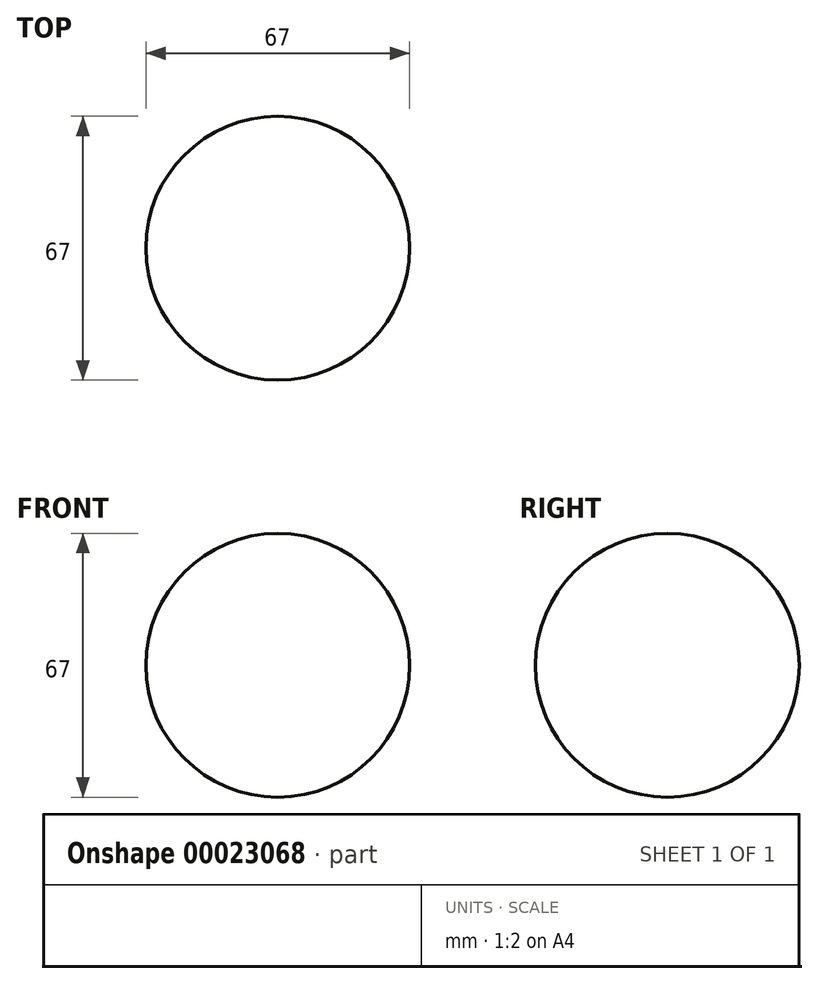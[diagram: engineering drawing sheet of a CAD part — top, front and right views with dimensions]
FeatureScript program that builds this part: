
annotation { "Feature Type Name" : "Feature", "Feature Type Description" : "" }
export const myFeature = defineFeature(function(context is Context, id is Id, definition is map)
    precondition{}
    {
        {
            var Q0;
            Q0=qCreatedBy(makeId("Front.planeOp"),FACE);
            var sketch = newSketch(context, id + "F0", { "sketchPlane" : qUnion([Q0])});
            skLineSegment(sketch, "E0.bottom", {"start": v(-22.5, 13) * mm, "end": v(22.5, 13) * mm});
            skLineSegment(sketch, "E0.top", {"start": v(-22.5, -13) * mm, "end": v(22.5, -13) * mm});
            skLineSegment(sketch, "E0.left", {"start": v(-22.5, 13) * mm, "end": v(-22.5, -13) * mm});
            skLineSegment(sketch, "E0.right", {"start": v(22.5, 13) * mm, "end": v(22.5, -13) * mm});
            skPoint(sketch, "E1", {"position": v(0, 13) * mm});
            skPoint(sketch, "E2", {"position": v(22.5, 0) * mm});
            skArc(sketch, "E3", {"start": v(0, 33.5) * mm, "mid": v(-33.5, 0) * mm, "end": v(0, -33.5) * mm});
            skLineSegment(sketch, "E4", {"start": v(0, 33.5) * mm, "end": v(0, -33.5) * mm});
            skSolve(sketch);
        }
        {
            var Q0;
            {var subQ1=sQuery(id+"F0.wireOp",EDGE,"E0.left");Q0=makeQuery(id+"F0.imprint","IMPRINT",FACE,{"disambiguationData":[TD([[makeQuery(id+"F0.imprint","IMPRINT",EDGE,{"derivedFrom":subQ1}),-1.0]])]});}
            var Q1;
            {var subQ0=sQuery(id+"F0.wireOp",EDGE,"E0.left");Q1=makeQuery(id+"F0.imprint","IMPRINT",FACE,{"disambiguationData":[TD([[makeQuery(id+"F0.imprint","IMPRINT",EDGE,{"derivedFrom":subQ0}),1.0]])]});}
            var Q2;
            Q2=sQuery(id+"F0.wireOp",EDGE,"E4");
            revolve(context, id + "F1", {"entities" : qUnion([Q0, Q1]), "axis" : qUnion([Q2]), "revolveType" : RevolveType.FULL});
        }
        {
            var Q0;
            {var subQ0=sQuery(id+"F0.wireOp",EDGE,"E0.left");Q0=makeQuery(id+"F0.imprint","IMPRINT",FACE,{"disambiguationData":[TD([[makeQuery(id+"F0.imprint","IMPRINT",EDGE,{"derivedFrom":subQ0}),1.0]])]});}
            var Q1;
            {var subQ0=sQuery(id+"F0.wireOp",EDGE,"E0.right");Q1=makeQuery(id+"F0.imprint","IMPRINT",FACE,{"disambiguationData":[TD([[makeQuery(id+"F0.imprint","IMPRINT",EDGE,{"derivedFrom":subQ0}),-1.0]])]});}
            extrude(context, id + "F2", {"entities" : qUnion([Q0, Q1]), "endBound" : BoundingType.SYMMETRIC, "oppositeDirection" : true, "depth" : 18 * mm});
        }
        {
            var Q0;
            Q0=makeQuery(id+"F2.opExtrude","SWEPT_FACE",FACE,{"disambiguationData":[OSD([sQuery(id+"F0.wireOp",EDGE,"E0.left")])]});
            var sketch = newSketch(context, id + "F3", { "sketchPlane" : qUnion([Q0])});
            skLineSegment(sketch, "E5.bottom", {"start": v(-6.72, -5.42) * mm, "end": v(6.72, -5.42) * mm});
            skLineSegment(sketch, "E5.top", {"start": v(-6.72, 5.42) * mm, "end": v(6.72, 5.42) * mm});
            skLineSegment(sketch, "E5.left", {"start": v(-6.72, -5.42) * mm, "end": v(-6.72, 5.42) * mm});
            skLineSegment(sketch, "E5.right", {"start": v(6.72, -5.42) * mm, "end": v(6.72, 5.42) * mm});
            skArc(sketch, "E6", {"start": v(-6.72, -5.42) * mm, "mid": v(0, -12.14) * mm, "end": v(6.72, -5.42) * mm});
            skArc(sketch, "E7", {"start": v(-6.72, 5.42) * mm, "mid": v(0, 12.14) * mm, "end": v(6.72, 5.42) * mm});
            skSolve(sketch);
        }
        {
            var Q0;
            Q0 = qSketchRegion(id + "F3", true);
            extrude(context, id + "F4", {"entities" : qUnion([Q0]), "operationType" : NewBodyOperationType.ADD, "depth" : 7 * mm});
        }
    });
